# Revit family: PRD_AR_WllMntdBbTps_F3SSelfClosingWashbasinTap_F3SV10091
name_source: partatom
category: Plumbing Fixtures
units: mm (PartAtom-declared; Revit-internal decimal feet)

## family parameters
Cut with Voids When Loaded = Yes
Enable Cutting in Views = Yes
Host = Face
Maintain Annotation Orientation = No
OmniClass Number = 23.45.05.14.99
OmniClass Title = Other Sanitary Washing Plumbing Fixtures
Part Type = Normal
Room Calculation Point = No
Round Connector Dimension = Use Diameter
Shared = No

## types (1)
- F3SV1009
    AccentColour = chrome-look (glossy)
    AdjustableFlowTime = Yes
    AssetType = Fixed
    BIMObjectName = PRD_AR_WallMountedBibTaps_F3SSelfClosingWashbasinTap_F3SV1009
    Basic colour = stainless steel-look
    BodyMaterial = PRD_AR_StainlessSteel_Brushed
    BuiltInFittingModel = Finishing section
    ButtonMaterial = PRD_AR_ChromatedBrass_HighPolished
    CW Connection = Yes
    CWFU = 0
    Category = Pr_40_20_87_93, Wall-mounted bib taps
    CloseOffRating = 0.0 Pa
    Color = stainless steel-look
    CompatibleA3000Open = No
    CoverPlateHeight = 245 mm
    CoverPlateWidth = 190 mm
    Default Elevation = 1219 mm
    Depressurised = No
    Description = F3S self-closing straight-way valve DN 15 for sanitary facilities, with remote control for concealed mounting. Especially suitable for facilities at risk of vandalism. Self-closing head part, hydraulically controlled for remote control, piston-free design, self-closing, for connection to pre-mixed hot water or cold water. All-metal construction, visible parts polished chromium-plated. Stainless steel cover plate 190 x 245 x 2 mm for invisible mounting via threaded rods up to a wall thickness of 50 to 500 mm, with recess for KWC wall outlet DN 15 (required separately), pre-mounted push-button actuation. Flush-mounted box, hydraulic control lines with empty conduit (2 m) and mounting material. Connection and maintenance via service room.
    DiameterNominal = DN 15
    Export Type to IFC As = IfcValveType
    Features = All-metal construction, visible parts polished chromium-plated. Stainless steel cover plate 190 x 245 x 2 mm. Wall outlet must be ordered separately.
    Finish = Satin finished
    FlowCoefficient = 0
    FunctionalPrinciple = hydraulic self-closing
    HW Connection = Yes
    HWFU = 0
    HygieneFlushing = No
    IfcExportAs = IfcValveType
    IfcExportType = USERDEFINED
    InletSize = G 1/2 B
    LockingMechanism = Top section, non-ceramic
    Manufacturer = KWC Group Management AG
    ManufacturerName = KWC Group Management AG
    ManufacturerURL = www.kwc-professional.com
    Material = stainless steel
    MaterialCasing = Stainless steel
    MaterialCodeCasing = 1.4301 Chrome Nickel steel V2A
    MaterialFitting = brass-look
    MaximumFlowTime = 20 Seconds
    MinimumFlowPressure = 1 bar
    MinimumFlowTime = 10 Seconds
    Model = F3SV1009
    ModelNumber = 2030067876
    ModelReference = F3SV1009
    NBSDescription = Taps and water supply fittings for sinks
    NBSReference = 45-35-70/345
    Name = F3S Self-closing washbasin tap F3SV1009
    NominalDepth = 2 mm  [stored 0.00656168 ft]
    NominalHeight = 245 mm  [stored 0.803806 ft]
    NominalWidth = 190 mm  [stored 0.62336 ft]
    PopUpWasteSet = No
    ProductInformation = http://pim.kwc.com
    ProtectiveShutdown = No
    Size = 15
    SoundInsulation = No
    Spout = Fixed
    Status = New
    SurfaceFinishCasing = satin finished
    SurfaceFinishFitting = Raw
    SurfaceTreatmentFitting = None
    TemperatureLimit = No
    TestPressure = 0.0 Pa
    ThermalDisinfection = No
    Type IFC Predefined Type = FLUSHING
    TypeOfMixing = No
    TypeOfMounting = Concealed
    TypeOfOperation = Manual operation
    TypeOfTap = Bib tap
    URL = www.kwc-professional.com
    Uniclass2015Code = Pr_40_20_87_93
    Uniclass2015Title = Wall-mounted bib taps
    Uniclass2015Version = Products v1.36
    ValveMechanism = OTHER
    ValveOperation = HYDRAULIC
    ValvePattern = STRAIGHT_2_PORT
    Vent Connection = Yes
    Version = 1
    VolumeFlowRateAt3Bar = 0.3 l/s
    WFU = 0
    Waste Connection = Yes
    WaterConnection = threaded connection (internal)
    WithRosettesCoverPlate = Yes
    WithTransformerPowerSupply = No
    WorkingPressure = 0.0 Pa

note: [stored X ft] marks values corroborated as IEEE doubles in the binary element streams (Revit-internal decimal feet)

## geometry (parser evidence)
native form markers: Sweep x6
no freeform markers — native parametric forms only
